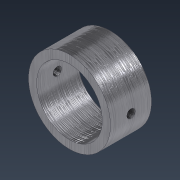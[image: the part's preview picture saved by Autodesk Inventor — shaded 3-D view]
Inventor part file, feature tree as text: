
AUTODESK INVENTOR PART (.ipt)
format: ipt  version: 2022 (Build 260153000, 153)  size: 119,808 bytes
history: native  units: mm
features: extrude x2, sketch x2
ambient origin geometry x8: Origin, YZ Plane, XZ Plane, XY Plane, X Axis, Y Axis, Z Axis, Center Point
bodies: Solid1 (feature_tree)
feature tree (4):
  extrude  "Extrusion1"  Depth=50.0mm
  extrude  "Extrusion2"  Depth=12.5mm
  sketch  "Sketch1"  dims[d0=40.0mm d1=50.0mm]
  sketch  "Sketch2"  dims[d2=25.0mm d3=0.0mm d4=12.5mm d5=5.0mm d6=23.0mm d7=0.0mm]
